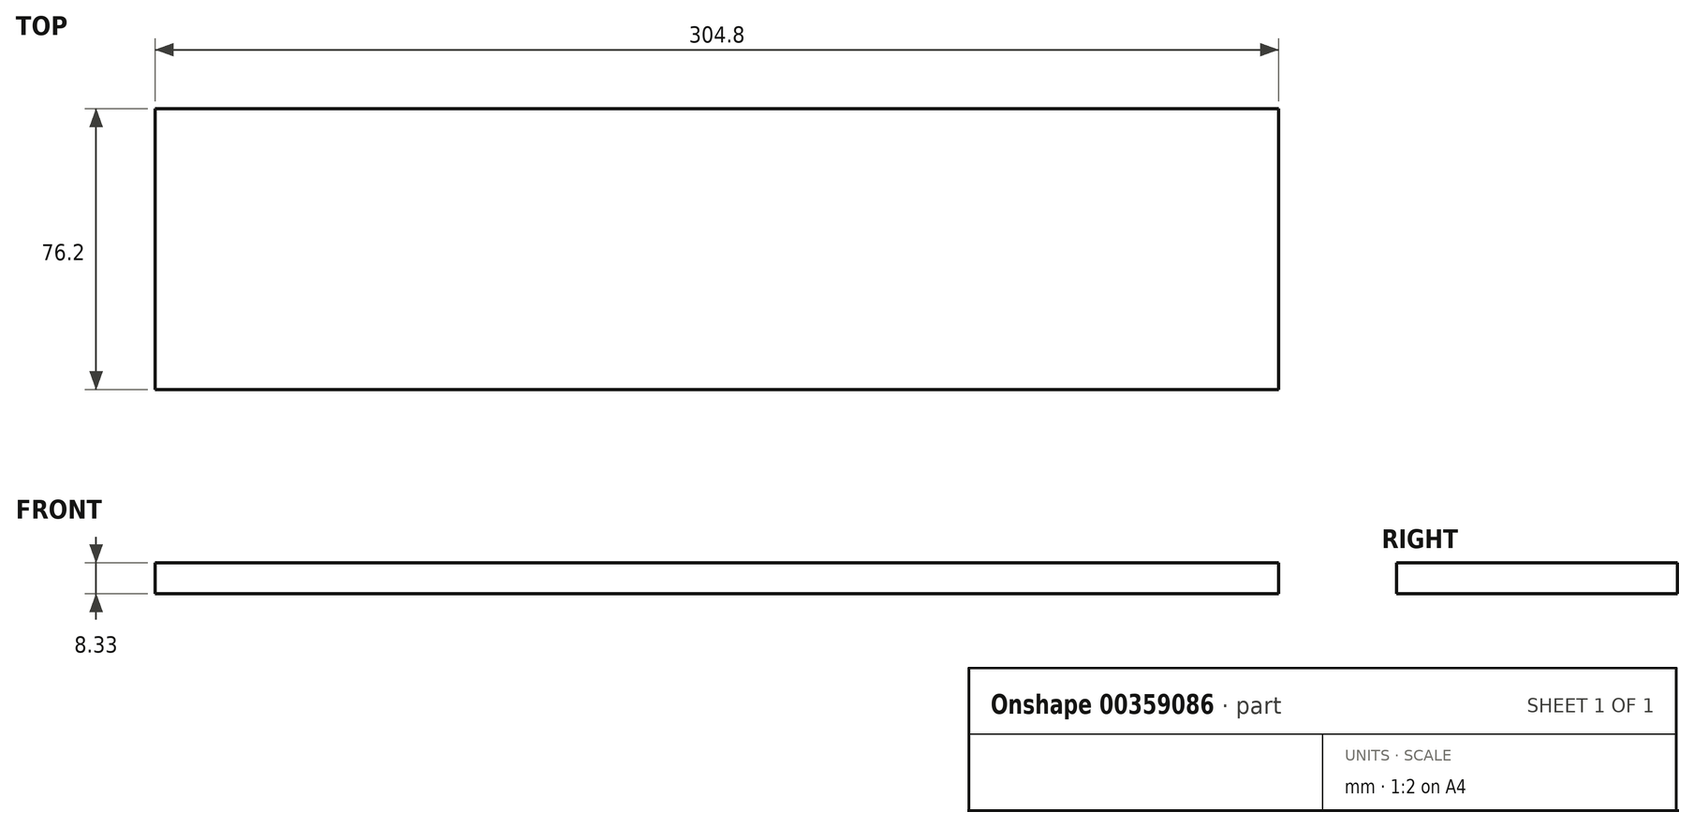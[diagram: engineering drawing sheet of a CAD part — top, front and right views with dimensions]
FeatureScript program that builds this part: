
annotation { "Feature Type Name" : "Feature", "Feature Type Description" : "" }
export const myFeature = defineFeature(function(context is Context, id is Id, definition is map)
    precondition{}
    {
        {
            var Q0;
            Q0=qCreatedBy(makeId("Front.planeOp"),FACE);
            var sketch = newSketch(context, id + "F0", { "sketchPlane" : qUnion([Q0])});
            skLineSegment(sketch, "E0", {"start": v(-67.25, 22.77) * mm, "end": v(-20.75, 22.77) * mm});
            skLineSegment(sketch, "E1", {"start": v(-58.97, 16.6) * mm, "end": v(-58.97, 5.94) * mm});
            skLineSegment(sketch, "E2.bottom", {"start": v(-350.95, 36.21) * mm, "end": v(-46.15, 36.21) * mm});
            skLineSegment(sketch, "E2.top", {"start": v(-350.95, 27.88) * mm, "end": v(-46.15, 27.88) * mm});
            skLineSegment(sketch, "E2.left", {"start": v(-350.95, 36.21) * mm, "end": v(-350.95, 27.88) * mm});
            skLineSegment(sketch, "E2.right", {"start": v(-46.15, 36.21) * mm, "end": v(-46.15, 27.88) * mm});
            skLineSegment(sketch, "E3", {"start": v(-33.37, 32.52) * mm, "end": v(-7.97, 32.52) * mm});
            skLineSegment(sketch, "E4", {"start": v(-7.97, 32.52) * mm, "end": v(-2.8, 20.92) * mm});
            skSolve(sketch);
        }
        {
            var Q0;
            Q0=sQuery(id+"F0.wireOp",EDGE,"E0");
            extrude(context, id + "F1", {"bodyType" : ToolBodyType.SURFACE, "surfaceEntities" : qUnion([Q0]), "depth" : 25.4 * mm});
        }
        {
            var Q0;
            Q0=makeQuery(id+"F0.imprint","IMPRINT",FACE,{"disambiguationData":[TD([[makeQuery(id+"F0.imprint","IMPRINT",EDGE,{"derivedFrom":sQuery(id+"F0.wireOp",EDGE,"E2.bottom")}),-1.0]])]});
            extrude(context, id + "F2", {"entities" : qUnion([Q0]), "depth" : 76.2 * mm});
        }
    });
